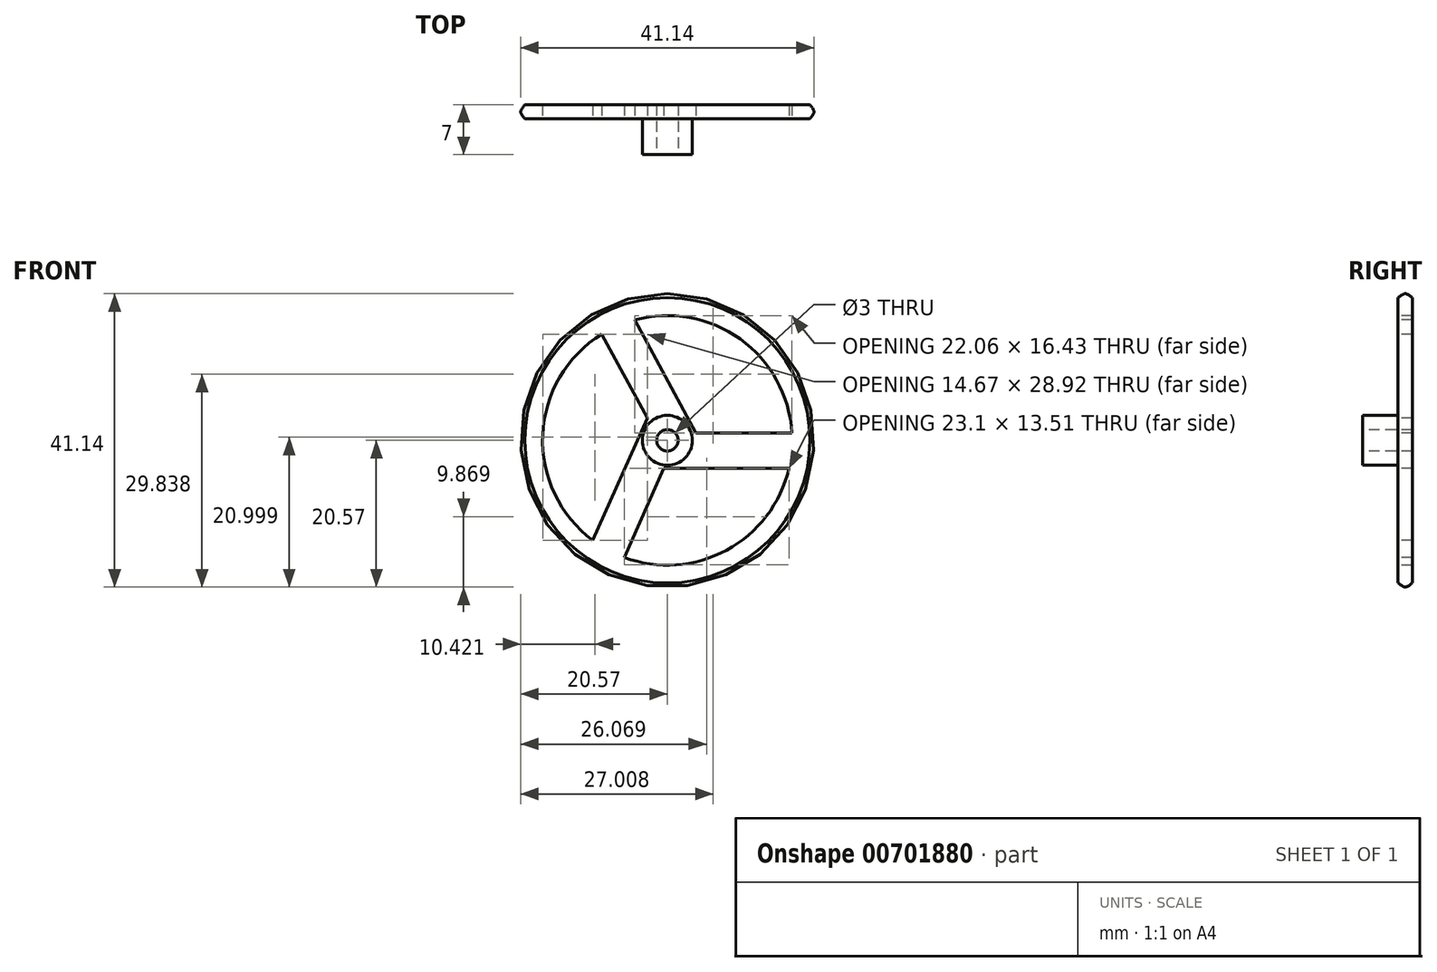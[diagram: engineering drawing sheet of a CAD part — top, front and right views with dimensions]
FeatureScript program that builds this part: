
annotation { "Feature Type Name" : "Feature", "Feature Type Description" : "" }
export const myFeature = defineFeature(function(context is Context, id is Id, definition is map)
    precondition{}
    {
        {
            var Q0;
            Q0=qCreatedBy(makeId("Top.planeOp"),FACE);
            var sketch = newSketch(context, id + "F0", { "sketchPlane" : qUnion([Q0])});
            skLineSegment(sketch, "E0", {"start": v(0, 0) * mm, "end": v(-20, 0) * mm});
            skLineSegment(sketch, "E1", {"start": v(-20, 2) * mm, "end": v(0, 2) * mm});
            skLineSegment(sketch, "E2", {"start": v(0, 2) * mm, "end": v(0, 0) * mm});
            skFitSpline(sketch, "E3", {"points": [v(-20, 2) * mm, v(-20.57, 1) * mm, v(-20, 0) * mm], "startDerivative": vector(-1.46, -1.95) * mm, "endDerivative": vector(1.45, -2.05) * mm});
            skSolve(sketch);
        }
        {
            var Q0;
            Q0=makeQuery(id+"F0.imprint","IMPRINT",FACE,{"disambiguationData":[TD([[makeQuery(id+"F0.imprint","IMPRINT",EDGE,{"derivedFrom":sQuery(id+"F0.wireOp",EDGE,"E0")}),-1.0]])]});
            var Q1;
            Q1=sQuery(id+"F0.wireOp",EDGE,"E2");
            revolve(context, id + "F1", {"entities" : qUnion([Q0]), "axis" : qUnion([Q1]), "revolveType" : RevolveType.FULL});
        }
        {
            var Q0;
            Q0=qCreatedBy(makeId("Front.planeOp"),FACE);
            var sketch = newSketch(context, id + "F2", { "sketchPlane" : qUnion([Q0])});
            skCircle(sketch, "E4", {"center": v(0, 0) * mm, "radius": 1.5 * mm});
            skCircle(sketch, "E5", {"center": v(0, 0) * mm, "radius": 3.5 * mm});
            skCircle(sketch, "E6", {"center": v(0, 0) * mm, "radius": 17.5 * mm});
            skSolve(sketch);
        }
        {
            var Q0;
            Q0=makeQuery(id+"F2.imprint","IMPRINT",FACE,{"disambiguationData":[TD([[makeQuery(id+"F2.imprint","IMPRINT",EDGE,{"derivedFrom":sQuery(id+"F2.wireOp",EDGE,"E4")}),1.0]])]});
            var Q1;
            Q1=makeQuery(id+"F2.imprint","IMPRINT",FACE,{"disambiguationData":[TD([[makeQuery(id+"F2.imprint","IMPRINT",EDGE,{"derivedFrom":sQuery(id+"F2.wireOp",EDGE,"E5")}),-1.0]])]});
            extrude(context, id + "F3", {"entities" : qUnion([Q0, Q1]), "operationType" : NewBodyOperationType.REMOVE, "endBound" : BoundingType.SYMMETRIC, "oppositeDirection" : true, "depth" : 1000 * mm, "offsetDistance" : 25 * mm});
        }
        {
            var Q0;
            Q0=qCreatedBy(makeId("Front.planeOp"),FACE);
            var sketch = newSketch(context, id + "F4", { "sketchPlane" : qUnion([Q0])});
            skLineSegment(sketch, "E7", {"start": v(-10.9, -15.01) * mm, "end": v(-6.33, -17.05) * mm});
            skLineSegment(sketch, "E8", {"start": v(18.92, -3.95) * mm, "end": v(18.92, 1.05) * mm});
            skLineSegment(sketch, "E9", {"start": v(-9.52, 15.48) * mm, "end": v(-5.12, 17.86) * mm});
            skLineSegment(sketch, "E10", {"start": v(-6.33, -17.05) * mm, "end": v(-0.5, -3.95) * mm});
            skLineSegment(sketch, "E11", {"start": v(-0.5, -3.95) * mm, "end": v(18.92, -3.95) * mm});
            skLineSegment(sketch, "E12", {"start": v(-5.12, 17.86) * mm, "end": v(4, 1.05) * mm});
            skLineSegment(sketch, "E13", {"start": v(4, 1.05) * mm, "end": v(18.92, 1.05) * mm});
            skLineSegment(sketch, "E14", {"start": v(-9.52, 15.48) * mm, "end": v(-2.81, 3.13) * mm});
            skLineSegment(sketch, "E15", {"start": v(-10.9, -15.01) * mm, "end": v(-2.81, 3.13) * mm});
            skSolve(sketch);
        }
        {
            var Q0;
            Q0=makeQuery(id+"F4.imprint","IMPRINT",FACE,{"disambiguationData":[TD([[makeQuery(id+"F4.imprint","IMPRINT",EDGE,{"derivedFrom":sQuery(id+"F4.wireOp",EDGE,"E7")}),1.0]])]});
            extrude(context, id + "F5", {"entities" : qUnion([Q0]), "operationType" : NewBodyOperationType.ADD, "oppositeDirection" : true, "depth" : 2 * mm, "offsetDistance" : 25 * mm});
        }
        {
            var Q0;
            Q0=makeQuery(id+"F2.imprint","IMPRINT",FACE,{"disambiguationData":[TD([[makeQuery(id+"F2.imprint","IMPRINT",EDGE,{"derivedFrom":sQuery(id+"F2.wireOp",EDGE,"E4")}),1.0]])]});
            extrude(context, id + "F6", {"entities" : qUnion([Q0]), "operationType" : NewBodyOperationType.REMOVE, "endBound" : BoundingType.SYMMETRIC, "oppositeDirection" : true, "depth" : 10050 * mm, "offsetDistance" : 25 * mm});
        }
        {
            var Q0;
            Q0=makeQuery(id+"F2.imprint","IMPRINT",FACE,{"disambiguationData":[TD([[makeQuery(id+"F2.imprint","IMPRINT",EDGE,{"derivedFrom":sQuery(id+"F2.wireOp",EDGE,"E4")}),-1.0]])]});
            extrude(context, id + "F7", {"entities" : qUnion([Q0]), "operationType" : NewBodyOperationType.ADD, "depth" : 5 * mm, "offsetDistance" : 25 * mm});
        }
    });
